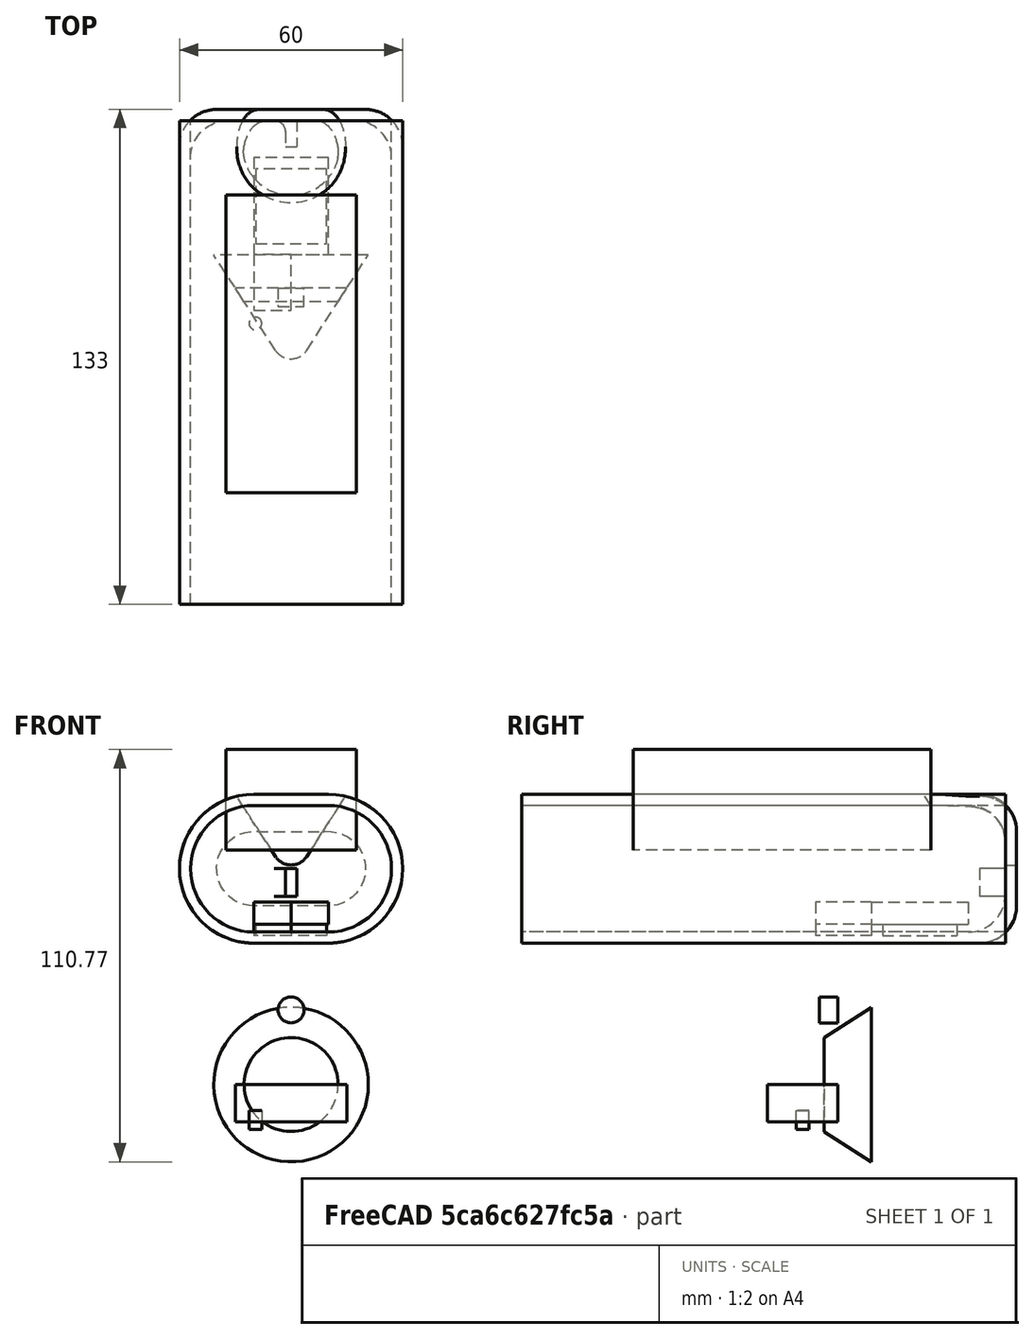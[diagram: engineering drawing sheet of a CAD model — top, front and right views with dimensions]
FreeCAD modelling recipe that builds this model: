
FCSTD DOCUMENT  (FreeCAD 0.16R6700 (Git))
Label: fuselage_simple
License: All rights reserved
LicenseURL: http://en.wikipedia.org/wiki/All_rights_reserved
objects: Sketcher::SketchObject×11, PartDesign::Pad×6, PartDesign::Fillet×3, PartDesign::Pocket×3, Mesh::Feature×1, PartDesign::Groove×1, App::MeasureDistance×1
note: 34 computed .brp shape members not serialized (recipe doc carries the construction recipe); baked Part::Feature solids carry a one-line shape summary decoded from their .brp

FEATURE [Mesh::Feature] cam_holder  label="cam+holder"
  Placement = pos=(6.5,55,0) rot=(0,0.707107,0.707107;3.14159rad)
FEATURE [Sketcher::SketchObject] Sketch
  Placement = pos=(0,0,0) rot=(1,0,0;1.5708rad)
  sketch-geometry (13):
    g0: ArcOfCircle CenterX=-10 CenterY=0 CenterZ=0 NormalX=0 NormalY=0 NormalZ=1 Radius=20 StartAngle=1.5708 EndAngle=4.71239
    g1: ArcOfCircle CenterX=10 CenterY=0 CenterZ=0 NormalX=0 NormalY=0 NormalZ=1 Radius=20 StartAngle=4.71239 EndAngle=7.85398
    g2: LineSegment StartX=-10 StartY=-20 StartZ=0 EndX=10 EndY=-20 EndZ=0
    g3: LineSegment StartX=-10 StartY=20 StartZ=0 EndX=10 EndY=20 EndZ=0
    g4: GeomPoint [constr] X=-30 Y=0 Z=0
    g5: GeomPoint [constr] X=30 Y=0 Z=0
    g6: LineSegment [constr] StartX=-10 StartY=0 StartZ=0 EndX=10 EndY=0 EndZ=0
    g7: ArcOfCircle CenterX=-10 CenterY=0 CenterZ=0 NormalX=0 NormalY=0 NormalZ=1 Radius=17 StartAngle=1.5708 EndAngle=4.71239
    g8: ArcOfCircle CenterX=10 CenterY=0 CenterZ=0 NormalX=0 NormalY=0 NormalZ=1 Radius=17 StartAngle=4.71239 EndAngle=7.85398
    g9: LineSegment StartX=-10 StartY=-17 StartZ=0 EndX=10 EndY=-17 EndZ=0
    g10: LineSegment StartX=-10 StartY=17 StartZ=0 EndX=10 EndY=17 EndZ=0
    g11: GeomPoint [constr] X=-27 Y=0 Z=0
    g12: GeomPoint [constr] X=27 Y=0 Z=0
  constraints (30):
    c: Tangent(g0,g3) = 1.5708
    c: Tangent(g0,g2) = -1.5708
    c: Tangent(g2,g1) = -1.5708
    c: Tangent(g3,g1) = 1.5708
    c: Horizontal(g2)
    c: Equal(g0,g1)
    c: PointOnObject(g0,g-1)
    c: PointOnObject(g4,g-1)
    c: PointOnObject(g5,g-1)
    c: PointOnObject(g5,g1)
    c: PointOnObject(g4,g0)
    c: Distance(g4,g5) = 60
    c: Distance(g1,g1) = 40
    c: Coincident(g6,g0)
    c: Coincident(g6,g1)
    c: Symmetric(g0,g1,g-2)
    c: Tangent(g7,g10) = 1.5708
    c: Tangent(g7,g9) = -1.5708
    c: Tangent(g9,g8) = -1.5708
    c: Tangent(g10,g8) = 1.5708
    c: Horizontal(g9)
    c: Equal(g7,g8)
    c: PointOnObject(g7,g-1)
    c: PointOnObject(g11,g7)
    c: PointOnObject(g12,g8)
    c: PointOnObject(g12,g-1)
    c: PointOnObject(g11,g-1)
    c: Distance(g11,g4) = 3
    c: Distance(g12,g5) = 3
    c: DistanceY(g8,g1) = 3
FEATURE [PartDesign::Pad] Pad
  Length = 130
  Length2 = 100
  Midplane = true
  Placement = pos=(0,0,0) rot=(1,0,0;1.5708rad)
  Sketch = -> Sketch
  Type = 0
FEATURE [Sketcher::SketchObject] Sketch001
  ExternalGeometry = -> [Pad]
  Placement = pos=(0,65,0) rot=(-1,0,0;1.5708rad)
  Support = -> Pad [Face9]
  sketch-geometry (4):
    g0: ArcOfCircle CenterX=-10 CenterY=0 CenterZ=0 NormalX=0 NormalY=0 NormalZ=1 Radius=20 StartAngle=1.5708 EndAngle=4.71239
    g1: ArcOfCircle CenterX=10 CenterY=-1e-12 CenterZ=0 NormalX=0 NormalY=0 NormalZ=1 Radius=20 StartAngle=4.71239 EndAngle=7.85398
    g2: LineSegment StartX=-10 StartY=-20 StartZ=0 EndX=10 EndY=-20 EndZ=0
    g3: LineSegment StartX=-10 StartY=20 StartZ=0 EndX=10 EndY=20 EndZ=0
  constraints (9):
    c: Tangent(g0,g3) = 1.5708
    c: Tangent(g0,g2) = -1.5708
    c: Tangent(g2,g1) = -1.5708
    c: Tangent(g3,g1) = 1.5708
    c: Horizontal(g2)
    c: Equal(g0,g1)
    c: Coincident(g0,g-4)
    c: Coincident(g0,g-4)
    c: Coincident(g1,g-3)
FEATURE [PartDesign::Pad] Pad001
  Length = 3
  Length2 = 100
  Placement = pos=(0,0,0) rot=(1,0,0;1.5708rad)
  Sketch = -> Sketch001
  Type = 0
FEATURE [PartDesign::Fillet] Fillet
  Base = -> Pad001 [Edge24,Edge22,Edge20,Edge18]
  Placement = pos=(0,0,0) rot=(1,0,0;1.5708rad)
  Radius = 10
FEATURE [PartDesign::Fillet] Fillet001
  Base = -> Fillet [Edge34,Edge40,Edge39,Edge36]
  Placement = pos=(0,0,0) rot=(1,0,0;1.5708rad)
  Radius = 10
FEATURE [Sketcher::SketchObject] Sketch003
  Placement = pos=(0,68,0) rot=(-1,0,0;1.5708rad)
  Support = -> Fillet001 [Face9]
  sketch-geometry (4):
    g0: ArcOfCircle CenterX=0 CenterY=-6 CenterZ=0 NormalX=0 NormalY=0 NormalZ=1 Radius=5 StartAngle=0.573699 EndAngle=2.56789
    g1: LineSegment StartX=-4.19949 StartY=-3.28629 StartZ=0 EndX=-15 EndY=-20 EndZ=0
    g2: LineSegment StartX=4.19949 StartY=-3.28629 StartZ=0 EndX=15 EndY=-20 EndZ=0
    g3: LineSegment StartX=15 StartY=-20 StartZ=0 EndX=-15 EndY=-20 EndZ=0
  constraints (13):
    c: Coincident(g1,g0)
    c: Coincident(g2,g0)
    c: Tangent(g0,g1)
    c: Tangent(g2,g0)
    c: PointOnObject(g0,g-2)
    c: Radius(g0) = 5
    c: DistanceY(g0,g-1) = 6
    c: Coincident(g3,g2)
    c: Horizontal(g3)
    c: Coincident(g1,g3)
    c: DistanceY(g1,g-1) = 20
    c: Symmetric(g1,g2,g-2)
    c: Distance(g3) = 30
FEATURE [PartDesign::Pocket] Pocket
  Length = 10
  Placement = pos=(0,0,0) rot=(1,0,0;1.5708rad)
  Sketch = -> Sketch003
  Type = 0
FEATURE [Sketcher::SketchObject] Sketch005
  ExternalGeometry = -> [Pocket]
  Placement = pos=(0,58,0) rot=(-1,0,0;1.5708rad)
  Support = -> Pocket [Face3]
  sketch-geometry (4):
    g0: LineSegment StartX=12.628 StartY=-16.3293 StartZ=0 EndX=20.7692 EndY=-28.9277 EndZ=0
    g1: LineSegment StartX=12.628 StartY=-16.3293 StartZ=0 EndX=0 EndY=-16.3293 EndZ=0
    g2: LineSegment StartX=20.7692 StartY=-28.9277 StartZ=0 EndX=0 EndY=-28.9277 EndZ=0
    g3: LineSegment StartX=0 StartY=-16.3293 StartZ=0 EndX=0 EndY=-28.9277 EndZ=0
  constraints (11):
    c: Distance(g0) = 15
    c: Coincident(g1,g0)
    c: PointOnObject(g1,g-2)
    c: Horizontal(g1)
    c: Coincident(g2,g0)
    c: PointOnObject(g2,g-2)
    c: Horizontal(g2)
    c: Coincident(g3,g1)
    c: Coincident(g3,g2)
    c: PointOnObject(g-3,g0)
    c: Coincident(g0,g-3)
FEATURE [Sketcher::SketchObject] Sketch004
  ExternalGeometry = -> [Pocket]
  Placement = pos=(0,0,20) rot=(0,0,1;3.14159rad)
  Support = -> Pocket [Face2]
  sketch-geometry (2):
    g0: ArcOfCircle CenterX=1.67198e-07 CenterY=-58 CenterZ=0 NormalX=0 NormalY=0 NormalZ=1 Radius=14.6464 StartAngle=6.28318 EndAngle=9.42478
    g1: LineSegment [constr] StartX=-14.6464 StartY=-58 StartZ=0 EndX=-14.6464 EndY=-63 EndZ=0
  constraints (6):
    c: Coincident(g0,g-3)
    c: Coincident(g0,g-4)
    c: Coincident(g1,g0)
    c: Vertical(g1)
    c: Tangent(g1,g0)
    c: DistanceY(g1,g1) = 5
FEATURE [PartDesign::Groove] Groove
  Angle = 360
  Axis = (0,0,-1)
  Base = (0,58,0)
  Placement = pos=(0,0,0) rot=(1,0,0;1.5708rad)
  ReferenceAxis = -> Sketch005 [V_Axis]
  Sketch = -> Sketch005
FEATURE [Sketcher::SketchObject] Sketch006
  Placement = pos=(0,65,0) rot=(1,0,0;1.5708rad)
  Support = -> Groove [Face20]
  sketch-geometry (4):
    g0: LineSegment StartX=-1.5 StartY=0 StartZ=0 EndX=1.5 EndY=0 EndZ=0
    g1: LineSegment StartX=1.5 StartY=0 StartZ=0 EndX=1.5 EndY=-7.5 EndZ=0
    g2: LineSegment StartX=1.5 StartY=-7.5 StartZ=0 EndX=-1.5 EndY=-7.5 EndZ=0
    g3: LineSegment StartX=-1.5 StartY=-7.5 StartZ=0 EndX=-1.5 EndY=0 EndZ=0
  constraints (12):
    c: PointOnObject(g0,g-1)
    c: PointOnObject(g0,g-1)
    c: Coincident(g0,g1)
    c: Vertical(g1)
    c: Coincident(g1,g2)
    c: Horizontal(g2)
    c: Coincident(g2,g3)
    c: Coincident(g3,g0)
    c: Vertical(g3)
    c: Distance(g0) = 3
    c: Symmetric(g0,g0,g-2)
    c: DistanceY(g1,g1) = 7.5
FEATURE [PartDesign::Pad] Pad002
  Length = 7
  Length2 = 100
  Placement = pos=(0,0,0) rot=(1,0,0;1.5708rad)
  Sketch = -> Sketch006
  Type = 0
FEATURE [PartDesign::Fillet] Fillet002
  Base = -> Pad002 [Edge66,Edge69]
  Placement = pos=(0,0,0) rot=(1,0,0;1.5708rad)
  Radius = 3
FEATURE [Sketcher::SketchObject] Sketch007
  ExternalGeometry = -> [Fillet002]
  Placement = pos=(0,65,0) rot=(1,0,0;1.5708rad)
  Support = -> Fillet002 [Face1]
  sketch-geometry (1):
    g0: Circle CenterX=-9.59932 CenterY=10.5 CenterZ=0 NormalX=0 NormalY=0 NormalZ=1 Radius=1.7
  constraints (3):
    c: Radius(g0) = 1.7
    c: DistanceX(g0,g-3) = 3
    c: DistanceY(g-3,g0) = 3.5
FEATURE [PartDesign::Pocket] Pocket001
  Length = 5
  Placement = pos=(0,0,0) rot=(1,0,0;1.5708rad)
  Sketch = -> Sketch007
  Type = 0
FEATURE [Sketcher::SketchObject] Sketch008
  ExternalGeometry = -> [Pocket001]
  Placement = pos=(0,0,20) rot=(0,0,1;3.14159rad)
  Support = -> Pocket001 [Face29]
  sketch-geometry (2):
    g0: Circle CenterX=0 CenterY=-37.9386 CenterZ=0 NormalX=0 NormalY=0 NormalZ=1 Radius=3.5
    g1: GeomPoint [constr] X=0 Y=-44.9386 Z=0
  constraints (5):
    c: PointOnObject(g0,g-2)
    c: Radius(g0) = 3.5
    c: PointOnObject(g1,g-2)
    c: PointOnObject(g1,g-3)
    c: DistanceY(g1,g0) = 7
FEATURE [PartDesign::Pocket] Pocket002
  Length = 5
  Placement = pos=(0,0,0) rot=(1,0,0;1.5708rad)
  Sketch = -> Sketch008
  Type = 0
FEATURE [Sketcher::SketchObject] Sketch009
  Placement = pos=(10,55,-9) rot=(0,1,0;3.14159rad)
  sketch-geometry (8):
    g0: LineSegment StartX=0 StartY=0 StartZ=0 EndX=20 EndY=0 EndZ=0
    g1: LineSegment StartX=20 StartY=0 StartZ=0 EndX=20 EndY=-26 EndZ=0
    g2: LineSegment StartX=10 StartY=-26 StartZ=0 EndX=0 EndY=-26 EndZ=0
    g3: LineSegment StartX=0 StartY=-26 StartZ=0 EndX=0 EndY=0 EndZ=0
    g4: LineSegment StartX=20 StartY=-26 StartZ=0 EndX=20 EndY=-41 EndZ=0
    g5: LineSegment StartX=20 StartY=-41 StartZ=0 EndX=10 EndY=-41 EndZ=0
    g6: LineSegment StartX=10 StartY=-41 StartZ=0 EndX=10 EndY=-26 EndZ=0
    g7: LineSegment [constr] StartX=10 StartY=-26 StartZ=0 EndX=20 EndY=-26 EndZ=0
  constraints (22):
    c: Coincident(g0,g1)
    c: Coincident(g2,g3)
    c: Coincident(g3,g0)
    c: Horizontal(g0)
    c: Horizontal(g2)
    c: Vertical(g1)
    c: Vertical(g3)
    c: Distance(g0) = 20
    c: DistanceY(g1,g1) = 26
    c: Coincident(g4,g1)
    c: Vertical(g4)
    c: DistanceY(g4,g4) = 15
    c: Coincident(g5,g4)
    c: Horizontal(g5)
    c: Distance(g5) = 10
    c: Coincident(g6,g5)
    c: Vertical(g6)
    c: Coincident(g2,g6)
    c: Coincident(g7,g2)
    c: Coincident(g7,g1)
    c: Horizontal(g7)
    c: Coincident(g0,g-1)
FEATURE [PartDesign::Pad] Pad003
  Length = 6
  Length2 = 100
  Placement = pos=(10,55,-9) rot=(0,1,0;3.14159rad)
  Sketch = -> Sketch009
  Type = 0
FEATURE [Sketcher::SketchObject] Sketch010
  ExternalGeometry = -> [Pad003]
  Placement = pos=(10,55,-15) rot=(0,1,0;3.14159rad)
  Support = -> Pad003 [Face9]
  sketch-geometry (8):
    g0: LineSegment StartX=0.5 StartY=-3 StartZ=0 EndX=19.5 EndY=-3 EndZ=0
    g1: LineSegment StartX=19.5 StartY=-3 StartZ=0 EndX=19.5 EndY=-23 EndZ=0
    g2: LineSegment StartX=19.5 StartY=-23 StartZ=0 EndX=0.5 EndY=-23 EndZ=0
    g3: LineSegment StartX=0.5 StartY=-23 StartZ=0 EndX=0.5 EndY=-3 EndZ=0
    g4: LineSegment StartX=10 StartY=-26 StartZ=0 EndX=20 EndY=-26 EndZ=0
    g5: LineSegment StartX=20 StartY=-26 StartZ=0 EndX=20 EndY=-41 EndZ=0
    g6: LineSegment StartX=20 StartY=-41 StartZ=0 EndX=10 EndY=-41 EndZ=0
    g7: LineSegment StartX=10 StartY=-26 StartZ=0 EndX=10 EndY=-41 EndZ=0
  constraints (21):
    c: Coincident(g0,g1)
    c: Coincident(g1,g2)
    c: Coincident(g2,g3)
    c: Coincident(g3,g0)
    c: Horizontal(g0)
    c: Horizontal(g2)
    c: Vertical(g1)
    c: Vertical(g3)
    c: Coincident(g4,g5)
    c: Coincident(g5,g6)
    c: Horizontal(g4)
    c: Horizontal(g6)
    c: Vertical(g5)
    c: Coincident(g4,g-3)
    c: Coincident(g5,g-4)
    c: Distance(g2) = 19
    c: Distance(g1) = 20
    c: DistanceX(g-1,g0) = 0.5
    c: DistanceY(g0,g-1) = 3
    c: Coincident(g7,g4)
    c: Coincident(g7,g6)
FEATURE [PartDesign::Pad] Pad004  label="video_tx"
  Length = 3
  Length2 = 100
  Placement = pos=(10,55,-9) rot=(0,1,0;3.14159rad)
  Sketch = -> Sketch010
  Type = 0
FEATURE [Sketcher::SketchObject] Sketch011
  Placement = pos=(-17.5,-35,5) rot=(0,0,1;0rad)
  sketch-geometry (4):
    g0: LineSegment StartX=0 StartY=80 StartZ=0 EndX=35 EndY=80 EndZ=0
    g1: LineSegment StartX=35 StartY=80 StartZ=0 EndX=35 EndY=0 EndZ=0
    g2: LineSegment StartX=35 StartY=0 StartZ=0 EndX=0 EndY=0 EndZ=0
    g3: LineSegment StartX=0 StartY=0 StartZ=0 EndX=0 EndY=80 EndZ=0
  constraints (11):
    c: Coincident(g0,g1)
    c: Coincident(g1,g2)
    c: Coincident(g2,g3)
    c: Coincident(g3,g0)
    c: Horizontal(g0)
    c: Horizontal(g2)
    c: Vertical(g1)
    c: Vertical(g3)
    c: Coincident(g2,g-1)
    c: Distance(g3) = 80
    c: Distance(g2) = 35
FEATURE [PartDesign::Pad] Pad005  label="battery"
  Length = 27
  Length2 = 100
  Placement = pos=(-17.5,-35,5) rot=(0,0,1;0rad)
  Sketch = -> Sketch011
  Type = 0
FEATURE [App::MeasureDistance] Distance  label="Distance: 49,9568 mm"
  Distance = 49.9568
  P1 = (24.8479,-65,-1.15504)
  P2 = (-24.8458,-59.8802,-1.19831)
